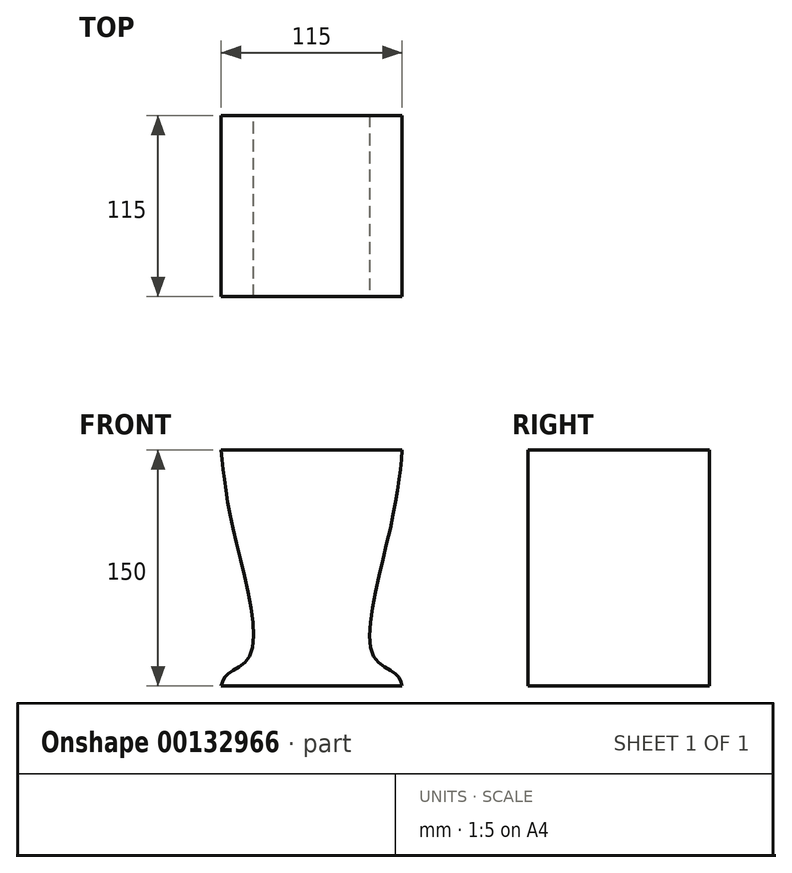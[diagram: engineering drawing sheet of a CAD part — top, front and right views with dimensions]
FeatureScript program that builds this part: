
annotation { "Feature Type Name" : "Feature", "Feature Type Description" : "" }
export const myFeature = defineFeature(function(context is Context, id is Id, definition is map)
    precondition{}
    {
        {
            var Q0;
            Q0=qCreatedBy(makeId("Front.planeOp"),FACE);
            var sketch = newSketch(context, id + "F0", { "sketchPlane" : qUnion([Q0])});
            skFitSpline(sketch, "E0.0", {"points": [v(-197.63, 64.03) * mm, v(-190.19, 14.81) * mm, v(-179.08, -66.17) * mm, v(-193.75, -78.43) * mm, v(-197.63, -85.97) * mm]});
            skFitSpline(sketch, "E1.0", {"points": [v(-82.63, 64.03) * mm, v(-90.08, 14.81) * mm, v(-101.19, -66.17) * mm, v(-86.52, -78.43) * mm, v(-82.63, -85.97) * mm]});
            skLineSegment(sketch, "E2", {"start": v(-140.13, -75.02) * mm, "end": v(-140.13, 64.03) * mm, "construction": true});
            skLineSegment(sketch, "E3", {"start": v(-197.63, 64.03) * mm, "end": v(-82.63, 64.03) * mm});
            skLineSegment(sketch, "E4", {"start": v(-82.63, -85.97) * mm, "end": v(-197.63, -85.97) * mm});
            skLineSegment(sketch, "E5", {"start": v(-197.63, 64.03) * mm, "end": v(-197.63, -85.97) * mm});
            skLineSegment(sketch, "E6", {"start": v(-82.63, 64.03) * mm, "end": v(-82.63, -85.97) * mm});
            skSolve(sketch);
        }
        {
            var Q0;
            Q0=makeQuery(id+"F0.imprint","IMPRINT",FACE,{"disambiguationData":[TD([[makeQuery(id+"F0.imprint","IMPRINT",EDGE,{"derivedFrom":sQuery(id+"F0.wireOp",EDGE,"E0.0")}),1.0]])]});
            extrude(context, id + "F1", {"entities" : qUnion([Q0]), "depth" : 115 * mm});
        }
        {
            var Q0;
            Q0=qCreatedBy(makeId("Right.planeOp"),FACE);
            var sketch = newSketch(context, id + "F2", { "sketchPlane" : qUnion([Q0])});
            skFitSpline(sketch, "E7.0", {"points": [v(-115, 64.03) * mm, v(-107.55, 14.81) * mm, v(-96.45, -66.17) * mm, v(-111.12, -78.43) * mm, v(-115, -85.97) * mm]});
            skLineSegment(sketch, "E8", {"start": v(-57.5, -85.97) * mm, "end": v(-57.5, 64.03) * mm});
            skFitSpline(sketch, "E9.0", {"points": [v(-115, 64.03) * mm, v(-115, 14.81) * mm, v(-115, -66.17) * mm, v(-115, -78.43) * mm, v(-115, -85.97) * mm], "construction": true});
            skFitSpline(sketch, "E10.0", {"points": [v(0, 64.03) * mm, v(0, 14.81) * mm, v(0, -66.17) * mm, v(0, -78.43) * mm, v(0, -85.97) * mm], "construction": true});
            skLineSegment(sketch, "E11", {"start": v(-115, 64.03) * mm, "end": v(-57.5, 64.03) * mm});
            skFitSpline(sketch, "E12.MirrorCS", {"points": [v(0, 64.03) * mm, v(-7.45, 14.81) * mm, v(-18.55, -66.17) * mm, v(-3.88, -78.43) * mm, v(0, -85.97) * mm]});
            skLineSegment(sketch, "E13.MirrorCS", {"start": v(0, 64.03) * mm, "end": v(-57.5, 64.03) * mm});
            skLineSegment(sketch, "E14", {"start": v(0, -85.97) * mm, "end": v(-115, -85.97) * mm});
            skLineSegment(sketch, "E15", {"start": v(0, -85.97) * mm, "end": v(0, 64.03) * mm});
            skLineSegment(sketch, "E16", {"start": v(-115, 64.03) * mm, "end": v(-115, -85.97) * mm});
            skSolve(sketch);
        }
        {
            var Q0;
            Q0=makeQuery(id+"F2.imprint","IMPRINT",FACE,{"disambiguationData":[TD([[makeQuery(id+"F2.imprint","IMPRINT",EDGE,{"derivedFrom":sQuery(id+"F2.wireOp",EDGE,"E7.0")}),-1.0]])]});
            var Q1;
            Q1=makeQuery(id+"F2.imprint","IMPRINT",FACE,{"disambiguationData":[TD([[makeQuery(id+"F2.imprint","IMPRINT",EDGE,{"derivedFrom":sQuery(id+"F2.wireOp",EDGE,"E12.MirrorCS")}),1.0]])]});
            extrude(context, id + "F3", {"entities" : qUnion([Q0, Q1]), "operationType" : NewBodyOperationType.REMOVE, "endBound" : BoundingType.SYMMETRIC, "oppositeDirection" : true, "depth" : 130 * mm});
        }
    });
